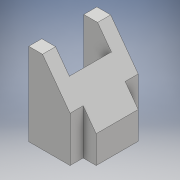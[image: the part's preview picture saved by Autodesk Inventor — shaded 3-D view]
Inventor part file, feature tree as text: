
AUTODESK INVENTOR PART (.ipt)
format: ipt  version: 2018 (Build 220112000, 112)  size: 135,168 bytes
history: native  units: mm
features: extrude x5, sketch x5
ambient origin geometry x8: Origin, YZ Plane, XZ Plane, XY Plane, X Axis, Y Axis, Z Axis, Center Point
bodies: Solid1 (feature_tree)
feature tree (10):
  extrude  "Extrusion1"  Depth=23.5mm
  extrude  "Extrusion2"  Depth=4.75mm
  extrude  "Extrusion7"  Depth=28.5mm TaperAngle=0.0deg
  extrude  "Extrusion8"  Depth=4.5mm TaperAngle=0.0deg
  extrude  "Extrusion9"  Depth=4.5mm TaperAngle=0.0deg
  sketch  "Sketch1"  dims[d0=18.75mm d1=23.5mm]
  sketch  "Sketch2"  dims[d2=28.5mm d3=0.0mm d4=4.75mm]
  sketch  "Sketch7"  dims[d5=9.5mm d6=28.5mm d7=0.0mm]
  sketch  "Sketch8"  dims[d27=4.5mm d28=4.5mm d29=0.0mm]
  sketch  "Sketch9"  dims[d30=4.5mm d31=4.5mm d32=0.0mm d33=9.5mm d34=0.0mm d35=0.0mm d36=4.5mm]
